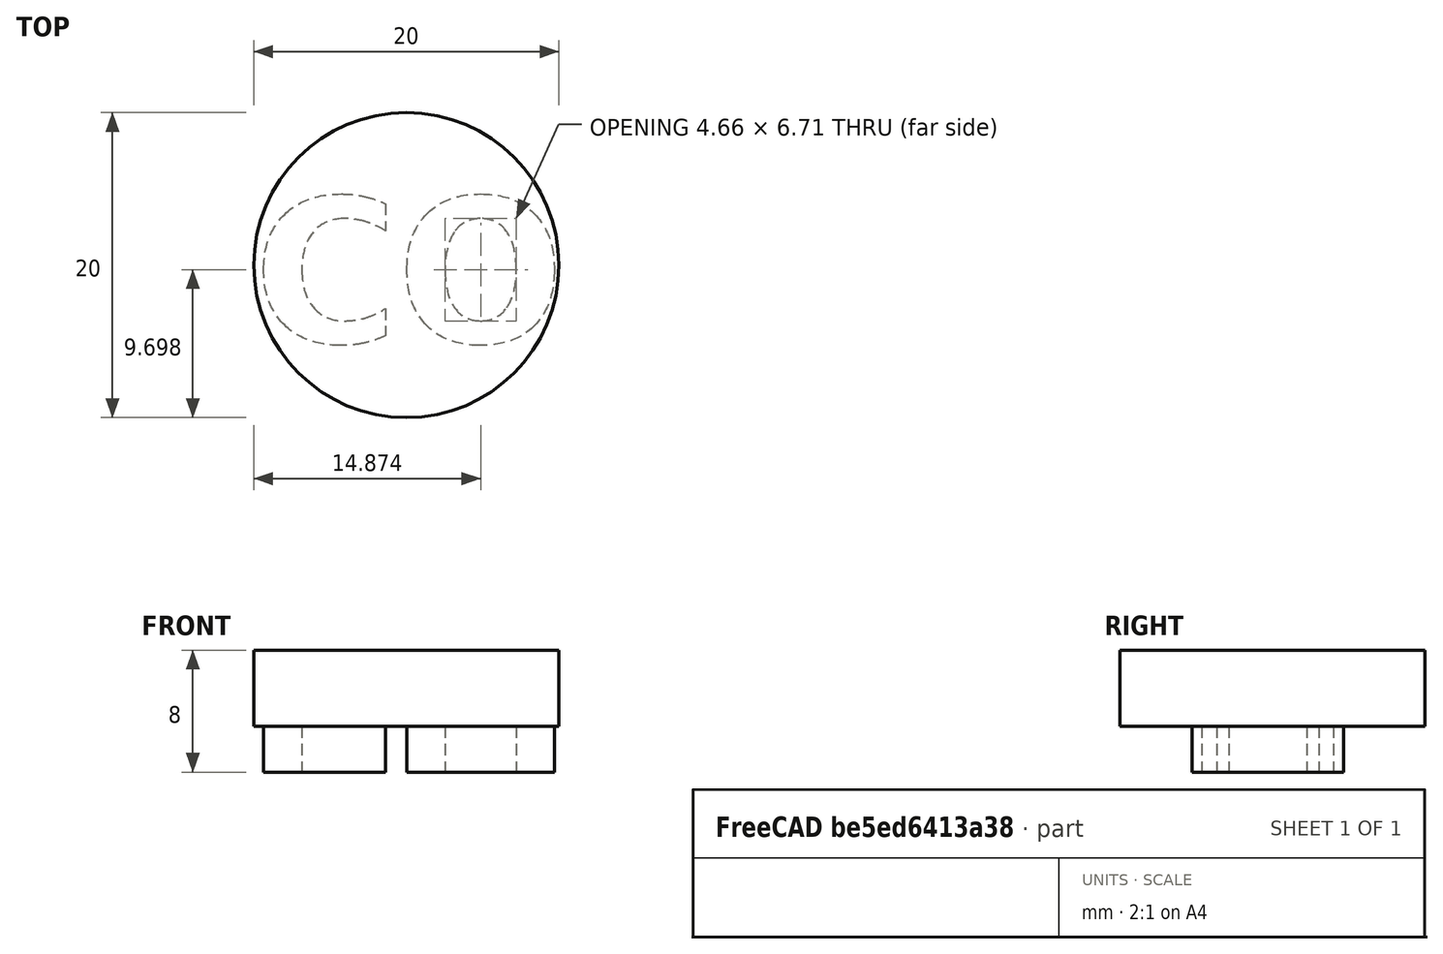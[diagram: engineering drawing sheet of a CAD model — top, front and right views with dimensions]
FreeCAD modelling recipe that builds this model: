
FCSTD DOCUMENT  (FreeCAD 0.20R27319 (Git))
Label: Stamp_C_O
License: All rights reserved
LicenseURL: http://en.wikipedia.org/wiki/All_rights_reserved
objects: Sketcher::SketchObject×1, PartDesign::Pad×1, PartDesign::Body×1, Part::Part2DObjectPython×1, Part::Extrusion×1
note: 6 computed .brp shape members not serialized (recipe doc carries the construction recipe); baked Part::Feature solids carry a one-line shape summary decoded from their .brp

FEATURE [Sketcher::SketchObject] Sketch
  FullyConstrained = true
  MapMode = 5
  Support = -> [XY_Plane]
  sketch-geometry (1):
    g0: Circle CenterX=0 CenterY=0 CenterZ=0 NormalX=0 NormalY=0 NormalZ=1 AngleXU=0 Radius=10
  constraints (2):
    c: Coincident(g0,g-1)
    c: Diameter(g0) = 20
FEATURE [PartDesign::Pad] Pad
  Direction = (0,0,1)
  Length = 5
  Length2 = 10
  Profile = -> Sketch
  ReferenceAxis = -> Sketch [N_Axis]
  Type = 0
FEATURE [PartDesign::Body] Body
  Group = -> [Sketch,Pad]
  Origin = -> Origin
  Tip = -> Pad
FEATURE [Part::Part2DObjectPython] ShapeString  # Draft 2D object (typed FeaturePython)
  FontFile = <path>
  MakeFace = true
  Placement = pos=(-10,-5,0) rot=(0,0,1;0rad)
  Size = 10
  String = CO
  Tracking = 0
FEATURE [Part::Extrusion] Extrude
  Base = -> ShapeString
  Dir = (0,0,1)
  DirMode = 2
  FaceMakerClass = Part::FaceMakerBullseye
  LengthFwd = -3
  LengthRev = 0
  Solid = false
  Symmetric = false
note: 1 file-system path scrubbed to <path> (originals preserved in the JSON sidecar)
